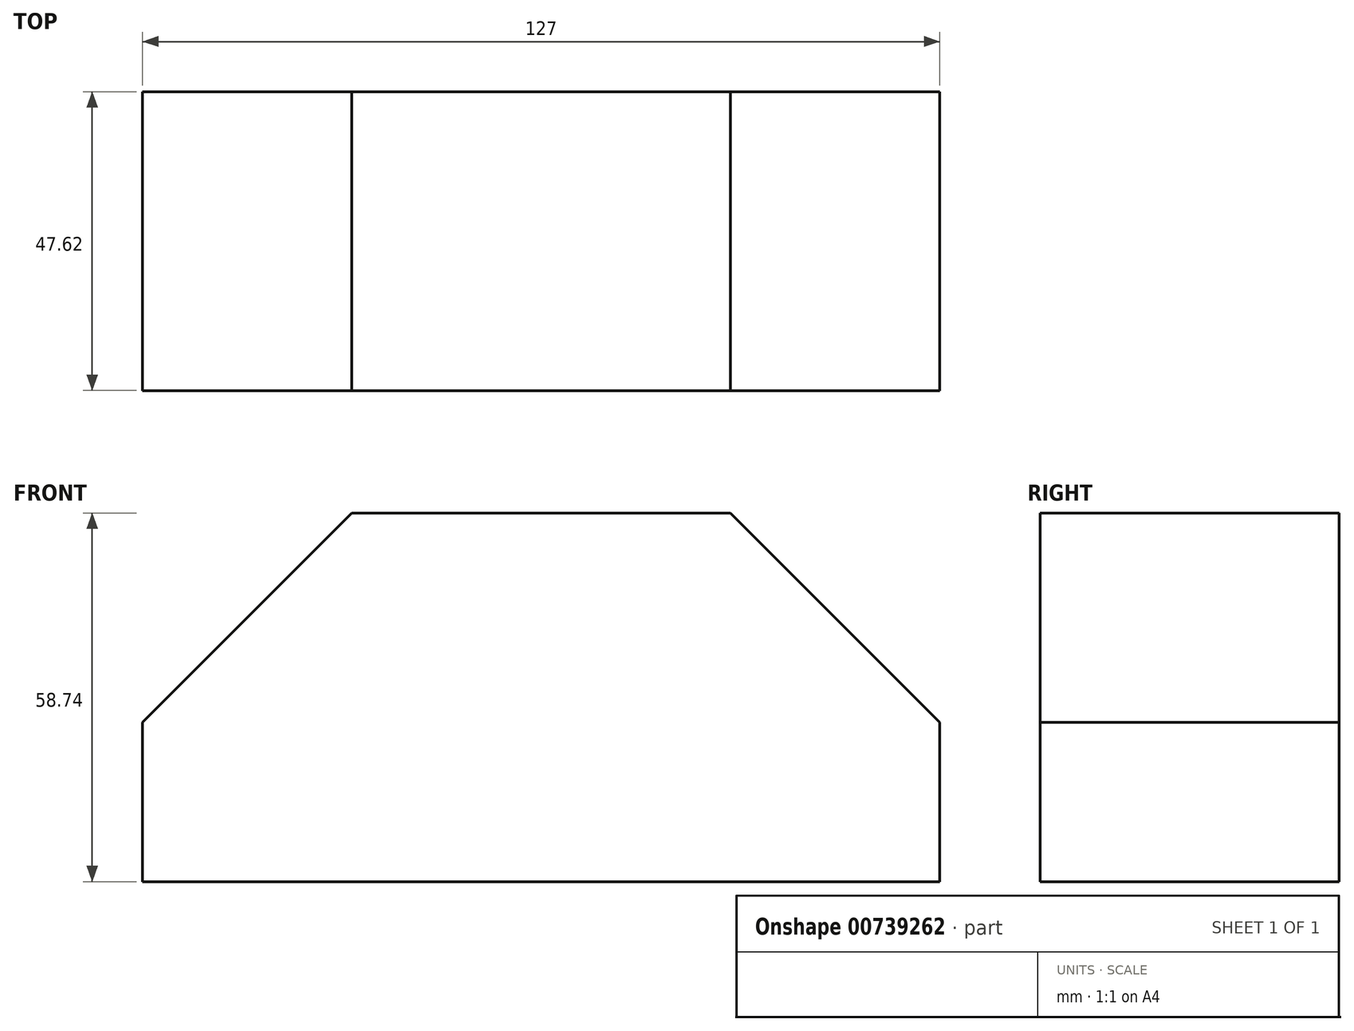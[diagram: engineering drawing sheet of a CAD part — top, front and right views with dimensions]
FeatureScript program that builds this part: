
annotation { "Feature Type Name" : "Feature", "Feature Type Description" : "" }
export const myFeature = defineFeature(function(context is Context, id is Id, definition is map)
    precondition{}
    {
        {
            var Q0;
            Q0=qCreatedBy(makeId("Front.planeOp"),FACE);
            var sketch = newSketch(context, id + "F0", { "sketchPlane" : qUnion([Q0])});
            skLineSegment(sketch, "E0", {"start": v(-62.06, 0) * mm, "end": v(64.94, 0) * mm});
            skLineSegment(sketch, "E1", {"start": v(64.94, 0) * mm, "end": v(64.94, 25.4) * mm});
            skLineSegment(sketch, "E2", {"start": v(64.94, 25.4) * mm, "end": v(31.6, 58.74) * mm});
            skLineSegment(sketch, "E3", {"start": v(31.6, 58.74) * mm, "end": v(-28.72, 58.74) * mm});
            skLineSegment(sketch, "E4", {"start": v(-28.72, 58.74) * mm, "end": v(-62.06, 25.4) * mm});
            skLineSegment(sketch, "E5", {"start": v(-62.06, 25.4) * mm, "end": v(-62.06, 0) * mm});
            skSolve(sketch);
        }
        {
            var Q0;
            Q0=makeQuery(id+"F0.imprint","IMPRINT",FACE,{"disambiguationData":[TD([[makeQuery(id+"F0.imprint","IMPRINT",EDGE,{"derivedFrom":sQuery(id+"F0.wireOp",EDGE,"E0")}),1.0]])]});
            extrude(context, id + "F1", {"entities" : qUnion([Q0]), "depth" : 47.62 * mm, "offsetDistance" : 25.4 * mm});
        }
    });
